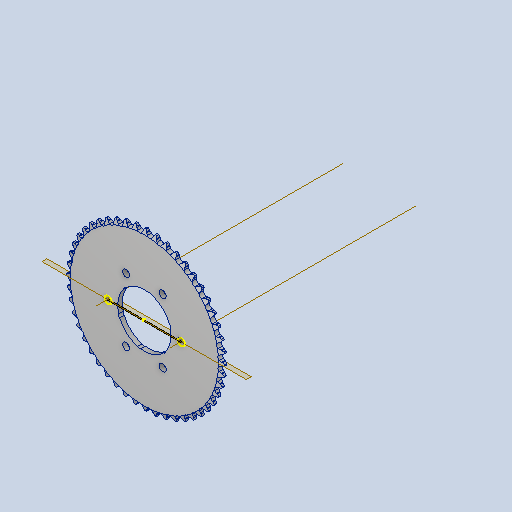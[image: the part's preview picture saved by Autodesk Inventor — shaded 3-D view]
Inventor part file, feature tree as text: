
AUTODESK INVENTOR PART (.ipt)
format: ipt  version: 2022.3 (Build 263350000, 350)  size: 1,150,464 bytes
history: native  units: in
note: dims shown in document units (in); Inventor stores cm internally (conversion verified against a paired STEP export)
features: sketch x3, other x2, extrude x1, hole x1, pattern_circular x1, plane x1, boolean_combine x1
ambient origin geometry x8: Origin, YZ Plane, XZ Plane, XY Plane, X Axis, Y Axis, Z Axis, Center Point
bodies: Solid1 (feature_tree)
feature tree (10):
  extrude  "Extrusion1"  TaperAngle=0.0deg  [1 undecoded]
  hole  "Hole2"  [1 undecoded]
  pattern_circular  "Circular Pattern1"  [2 undecoded]
  plane  "Work Plane1"
  sketch  "Sketch3"  dims[d15=0.266in d16=0.75in d17=0.375in d18=0.25in d19=0.5635in d20=1.0in d21=0.8108in d22=2.3622in d23=2.4737in]
  sketch  "Sketch1"  dims[d0=2.0in d1=0.0in d2=0.0in]
  sketch  "Sketch2"  dims[d3=2.75in]
  other  "Work Axis1"
  other  "Work Axis2"
  boolean_combine  "Combine1"
note: 4 required parameter values undecoded (feature->parameter linkage not recoverable at this tier; creation-order binding heuristic only, values carry confidence <= 0.55)
